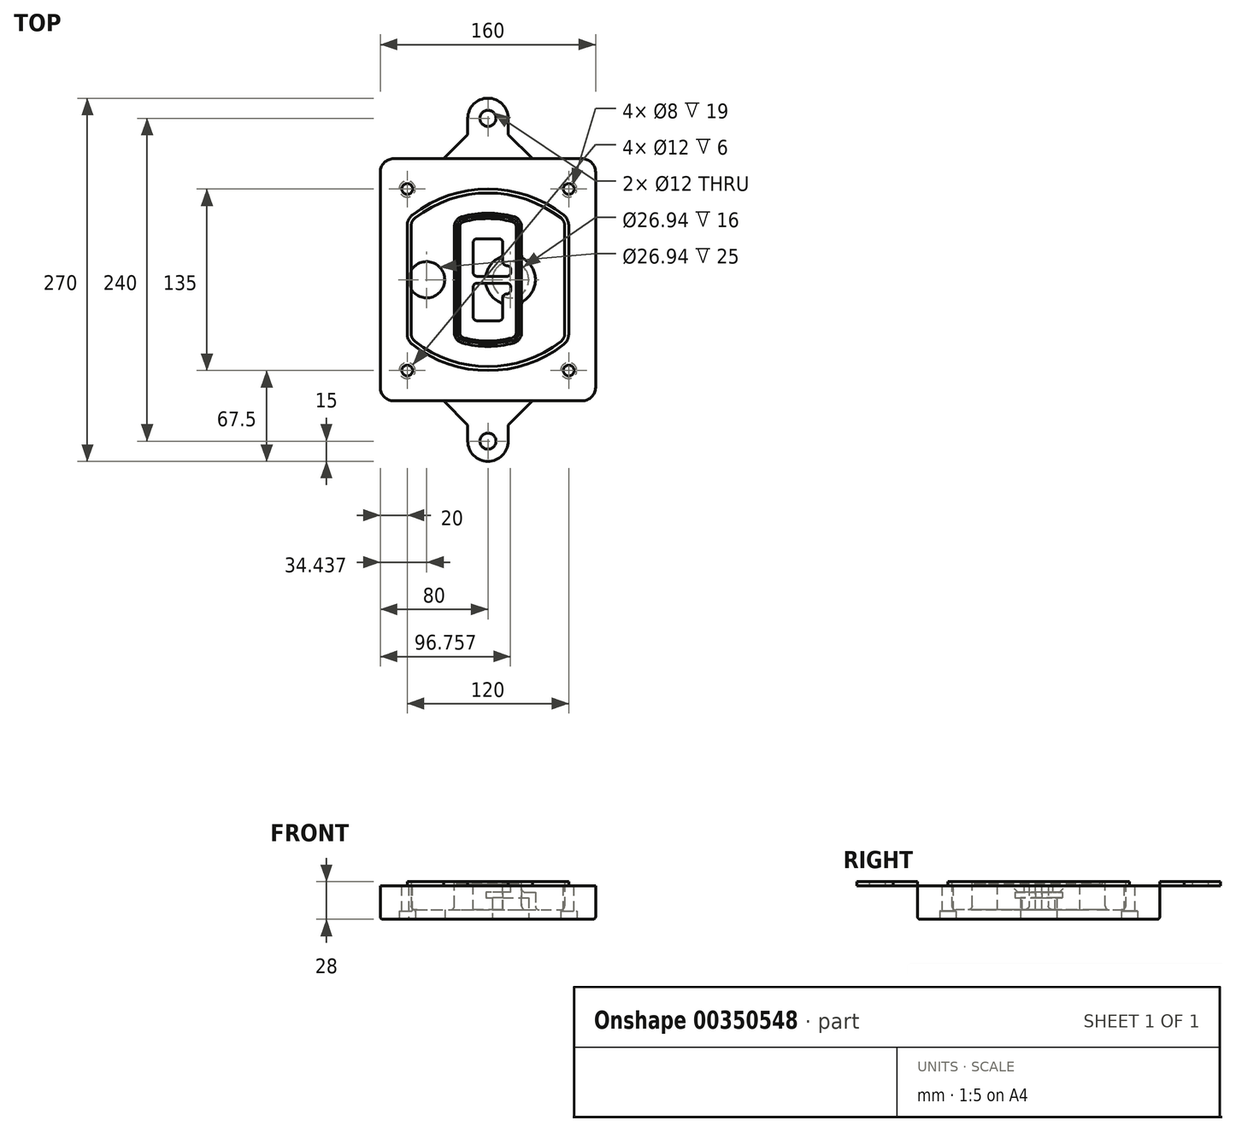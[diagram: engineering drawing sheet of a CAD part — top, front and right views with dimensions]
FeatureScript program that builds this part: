
annotation { "Feature Type Name" : "Feature", "Feature Type Description" : "" }
export const myFeature = defineFeature(function(context is Context, id is Id, definition is map)
    precondition{}
    {
        {
            var Q0;
            Q0=qCreatedBy(makeId("Top.planeOp"),FACE);
            var sketch = newSketch(context, id + "F0", { "sketchPlane" : qUnion([Q0])});
            skPoint(sketch, "E0.rect.middle", {"position": v(0, 0) * mm});
            skLineSegment(sketch, "E1.bottom", {"start": v(-70, -90) * mm, "end": v(70, -90) * mm});
            skLineSegment(sketch, "E1.top", {"start": v(-70, 90) * mm, "end": v(70, 90) * mm});
            skLineSegment(sketch, "E1.left", {"start": v(-80, -80) * mm, "end": v(-80, 80) * mm});
            skLineSegment(sketch, "E1.right", {"start": v(80, -80) * mm, "end": v(80, 80) * mm});
            skLineSegment(sketch, "E2", {"start": v(-80, 90) * mm, "end": v(80, -90) * mm, "construction": true});
            skLineSegment(sketch, "E3", {"start": v(80, 90) * mm, "end": v(-80, -90) * mm, "construction": true});
            skCircle(sketch, "E4", {"center": v(-60, 67.5) * mm, "radius": 4 * mm});
            skCircle(sketch, "E5", {"center": v(60, 67.5) * mm, "radius": 4 * mm});
            skCircle(sketch, "E6", {"center": v(60, -67.5) * mm, "radius": 4 * mm});
            skCircle(sketch, "E7", {"center": v(-60, -67.5) * mm, "radius": 4 * mm});
            skLineSegment(sketch, "E8", {"start": v(-60, 67.5) * mm, "end": v(60, 67.5) * mm, "construction": true});
            skLineSegment(sketch, "E9", {"start": v(60, 67.5) * mm, "end": v(60, -67.5) * mm, "construction": true});
            skLineSegment(sketch, "E10", {"start": v(60, -67.5) * mm, "end": v(-60, -67.5) * mm, "construction": true});
            skLineSegment(sketch, "E11", {"start": v(-60, -67.5) * mm, "end": v(-60, 67.5) * mm, "construction": true});
            skLineSegment(sketch, "E12", {"start": v(-60, 40.3) * mm, "end": v(-60, -40.3) * mm});
            skLineSegment(sketch, "E13", {"start": v(60, 40.3) * mm, "end": v(60, -40.3) * mm});
            skArc(sketch, "E14", {"start": v(56.15, 48.18) * mm, "mid": v(0, 67.5) * mm, "end": v(-56.15, 48.18) * mm});
            skArc(sketch, "E15", {"start": v(-56.15, -48.18) * mm, "mid": v(0, -67.5) * mm, "end": v(56.15, -48.18) * mm});
            skLineSegment(sketch, "E16", {"start": v(-60, 0) * mm, "end": v(60, 0) * mm, "construction": true});
            skPoint(sketch, "E17.visualSharp", {"position": v(-60, -45) * mm});
            skArc(sketch, "E17.filletArc", {"start": v(-60, -40.3) * mm, "mid": v(-58.99, -44.68) * mm, "end": v(-56.15, -48.18) * mm});
            skPoint(sketch, "E18.visualSharp", {"position": v(-60, 45) * mm});
            skArc(sketch, "E18.filletArc", {"start": v(-56.15, 48.18) * mm, "mid": v(-58.99, 44.68) * mm, "end": v(-60, 40.3) * mm});
            skPoint(sketch, "E19.visualSharp", {"position": v(60, 45) * mm});
            skArc(sketch, "E19.filletArc", {"start": v(60, 40.3) * mm, "mid": v(58.99, 44.68) * mm, "end": v(56.15, 48.18) * mm});
            skPoint(sketch, "E20.visualSharp", {"position": v(60, -45) * mm});
            skArc(sketch, "E20.filletArc", {"start": v(56.15, -48.18) * mm, "mid": v(58.99, -44.68) * mm, "end": v(60, -40.3) * mm});
            skPoint(sketch, "E21.visualSharp", {"position": v(-80, 90) * mm});
            skArc(sketch, "E21.filletArc", {"start": v(-70, 90) * mm, "mid": v(-77.07, 87.07) * mm, "end": v(-80, 80) * mm});
            skPoint(sketch, "E22.visualSharp", {"position": v(80, 90) * mm});
            skArc(sketch, "E22.filletArc", {"start": v(80, 80) * mm, "mid": v(77.07, 87.07) * mm, "end": v(70, 90) * mm});
            skPoint(sketch, "E23.visualSharp", {"position": v(80, -90) * mm});
            skArc(sketch, "E23.filletArc", {"start": v(70, -90) * mm, "mid": v(77.07, -87.07) * mm, "end": v(80, -80) * mm});
            skPoint(sketch, "E24.visualSharp", {"position": v(-80, -90) * mm});
            skArc(sketch, "E24.filletArc", {"start": v(-80, -80) * mm, "mid": v(-77.07, -87.07) * mm, "end": v(-70, -90) * mm});
            skArc(sketch, "E25.0", {"start": v(57, 40.3) * mm, "mid": v(56.3, 43.36) * mm, "end": v(54.3, 45.81) * mm});
            skLineSegment(sketch, "E25.1", {"start": v(57, 40.3) * mm, "end": v(57, -40.3) * mm});
            skArc(sketch, "E25.2", {"start": v(54.3, -45.81) * mm, "mid": v(56.3, -43.36) * mm, "end": v(57, -40.3) * mm});
            skArc(sketch, "E25.3", {"start": v(-54.3, -45.81) * mm, "mid": v(0, -64.5) * mm, "end": v(54.3, -45.81) * mm});
            skArc(sketch, "E25.4", {"start": v(-57, -40.3) * mm, "mid": v(-56.3, -43.36) * mm, "end": v(-54.3, -45.81) * mm});
            skArc(sketch, "E25.5", {"start": v(54.3, 45.81) * mm, "mid": v(0, 64.5) * mm, "end": v(-54.3, 45.81) * mm});
            skLineSegment(sketch, "E25.6", {"start": v(-57, 40.3) * mm, "end": v(-57, -40.3) * mm});
            skArc(sketch, "E25.7", {"start": v(-54.3, 45.81) * mm, "mid": v(-56.3, 43.36) * mm, "end": v(-57, 40.3) * mm});
            skArc(sketch, "E26.0", {"start": v(-58.62, 51.33) * mm, "mid": v(-62.58, 46.43) * mm, "end": v(-64, 40.3) * mm});
            skArc(sketch, "E26.1", {"start": v(58.62, 51.33) * mm, "mid": v(0, 71.5) * mm, "end": v(-58.62, 51.33) * mm});
            skArc(sketch, "E26.2", {"start": v(64, 40.3) * mm, "mid": v(62.58, 46.43) * mm, "end": v(58.62, 51.33) * mm});
            skLineSegment(sketch, "E26.3", {"start": v(64, 40.3) * mm, "end": v(64, -40.3) * mm});
            skArc(sketch, "E26.4", {"start": v(58.62, -51.33) * mm, "mid": v(62.58, -46.43) * mm, "end": v(64, -40.3) * mm});
            skLineSegment(sketch, "E26.5", {"start": v(-64, 40.3) * mm, "end": v(-64, -40.3) * mm});
            skArc(sketch, "E26.6", {"start": v(-58.62, -51.33) * mm, "mid": v(0, -71.5) * mm, "end": v(58.62, -51.33) * mm});
            skArc(sketch, "E26.7", {"start": v(-64, -40.3) * mm, "mid": v(-62.58, -46.43) * mm, "end": v(-58.62, -51.33) * mm});
            skSolve(sketch);
        }
        {
            var Q0;
            Q0=makeQuery(id+"F0.imprint","IMPRINT",FACE,{"disambiguationData":[TD([[makeQuery(id+"F0.imprint","IMPRINT",EDGE,{"derivedFrom":sQuery(id+"F0.wireOp",EDGE,"E1.bottom")}),1.0]])]});
            var Q1;
            Q1=makeQuery(id+"F0.imprint","IMPRINT",FACE,{"disambiguationData":[TD([[makeQuery(id+"F0.imprint","IMPRINT",EDGE,{"derivedFrom":sQuery(id+"F0.wireOp",EDGE,"E12")}),1.0]])]});
            var Q2;
            Q2=makeQuery(id+"F0.imprint","IMPRINT",FACE,{"disambiguationData":[TD([[makeQuery(id+"F0.imprint","IMPRINT",EDGE,{"derivedFrom":sQuery(id+"F0.wireOp",EDGE,"E25.0")}),1.0]])]});
            var Q3;
            Q3=makeQuery(id+"F0.imprint","IMPRINT",FACE,{"disambiguationData":[TD([[makeQuery(id+"F0.imprint","IMPRINT",EDGE,{"derivedFrom":sQuery(id+"F0.wireOp",EDGE,"E12")}),-1.0]])]});
            extrude(context, id + "F1", {"entities" : qUnion([Q0, Q1, Q2, Q3]), "oppositeDirection" : true, "depth" : 25 * mm});
        }
        {
            var Q0;
            Q0=makeQuery(id+"F0.imprint","IMPRINT",FACE,{"disambiguationData":[TD([[makeQuery(id+"F0.imprint","IMPRINT",EDGE,{"derivedFrom":sQuery(id+"F0.wireOp",EDGE,"E12")}),1.0]])]});
            extrude(context, id + "F2", {"entities" : qUnion([Q0]), "operationType" : NewBodyOperationType.ADD, "depth" : 3 * mm});
        }
        {
            var Q0;
            Q0=makeQuery(id+"F0.imprint","IMPRINT",FACE,{"disambiguationData":[TD([[makeQuery(id+"F0.imprint","IMPRINT",EDGE,{"derivedFrom":sQuery(id+"F0.wireOp",EDGE,"E25.0")}),1.0]])]});
            extrude(context, id + "F3", {"entities" : qUnion([Q0]), "operationType" : NewBodyOperationType.REMOVE, "oppositeDirection" : true, "depth" : 18 * mm});
        }
        {
            var Q0;
            Q0=makeQuery(id+"F2.opExtrude","CAP_FACE",FACE,{"disambiguationData":[OSD([sQuery(id+"F0.wireOp",EDGE,"E12"),sQuery(id+"F0.wireOp",EDGE,"E13"),sQuery(id+"F0.wireOp",EDGE,"E14"),sQuery(id+"F0.wireOp",EDGE,"E15"),sQuery(id+"F0.wireOp",EDGE,"E17.filletArc"),sQuery(id+"F0.wireOp",EDGE,"E18.filletArc"),sQuery(id+"F0.wireOp",EDGE,"E19.filletArc"),sQuery(id+"F0.wireOp",EDGE,"E20.filletArc"),sQuery(id+"F0.wireOp",EDGE,"E25.0"),sQuery(id+"F0.wireOp",EDGE,"E25.1"),sQuery(id+"F0.wireOp",EDGE,"E25.2"),sQuery(id+"F0.wireOp",EDGE,"E25.3"),sQuery(id+"F0.wireOp",EDGE,"E25.4"),sQuery(id+"F0.wireOp",EDGE,"E25.5"),sQuery(id+"F0.wireOp",EDGE,"E25.6"),sQuery(id+"F0.wireOp",EDGE,"E25.7")])],"isStart":false});
            var sketch = newSketch(context, id + "F4", { "sketchPlane" : qUnion([Q0])});
            skArc(sketch, "E27.0", {"start": v(-19.08, -46.97) * mm, "mid": v(0, -49.5) * mm, "end": v(19.08, -46.97) * mm});
            skArc(sketch, "E28.0", {"start": v(19.08, 46.97) * mm, "mid": v(0, 49.5) * mm, "end": v(-19.08, 46.97) * mm});
            skLineSegment(sketch, "E29", {"start": v(-25, 39.25) * mm, "end": v(-25, -39.25) * mm});
            skLineSegment(sketch, "E30", {"start": v(25, 39.25) * mm, "end": v(25, -39.25) * mm});
            skLineSegment(sketch, "E31", {"start": v(-25, 45.1) * mm, "end": v(25, 45.1) * mm, "construction": true});
            skLineSegment(sketch, "E32", {"start": v(-25, -45.1) * mm, "end": v(25, -45.1) * mm, "construction": true});
            skPoint(sketch, "E33.visualSharp", {"position": v(-25, 45.1) * mm});
            skArc(sketch, "E33.filletArc", {"start": v(-19.08, 46.97) * mm, "mid": v(-23.35, 44.11) * mm, "end": v(-25, 39.25) * mm});
            skPoint(sketch, "E34.visualSharp", {"position": v(25, 45.1) * mm});
            skArc(sketch, "E34.filletArc", {"start": v(25, 39.25) * mm, "mid": v(23.35, 44.11) * mm, "end": v(19.08, 46.97) * mm});
            skPoint(sketch, "E35.visualSharp", {"position": v(25, -45.1) * mm});
            skArc(sketch, "E35.filletArc", {"start": v(19.08, -46.97) * mm, "mid": v(23.35, -44.11) * mm, "end": v(25, -39.25) * mm});
            skPoint(sketch, "E36.visualSharp", {"position": v(-25, -45.1) * mm});
            skArc(sketch, "E36.filletArc", {"start": v(-25, -39.25) * mm, "mid": v(-23.35, -44.11) * mm, "end": v(-19.08, -46.97) * mm});
            skArc(sketch, "E37.0", {"start": v(54.3, 45.81) * mm, "mid": v(0, 64.5) * mm, "end": v(-54.3, 45.81) * mm});
            skArc(sketch, "E37.1", {"start": v(-54.3, 45.81) * mm, "mid": v(-56.3, 43.36) * mm, "end": v(-57, 40.3) * mm});
            skLineSegment(sketch, "E37.2", {"start": v(-57, 40.3) * mm, "end": v(-57, -40.3) * mm});
            skArc(sketch, "E37.3", {"start": v(-57, -40.3) * mm, "mid": v(-56.3, -43.36) * mm, "end": v(-54.3, -45.81) * mm});
            skArc(sketch, "E37.4", {"start": v(-54.3, -45.81) * mm, "mid": v(0, -64.5) * mm, "end": v(54.3, -45.81) * mm});
            skArc(sketch, "E37.5", {"start": v(54.3, -45.81) * mm, "mid": v(56.3, -43.36) * mm, "end": v(57, -40.3) * mm});
            skLineSegment(sketch, "E37.6", {"start": v(57, 40.3) * mm, "end": v(57, -40.3) * mm});
            skArc(sketch, "E37.7", {"start": v(57, 40.3) * mm, "mid": v(56.3, 43.36) * mm, "end": v(54.3, 45.81) * mm});
            skLineSegment(sketch, "E38.0", {"start": v(23, 39.25) * mm, "end": v(23, -39.25) * mm});
            skArc(sketch, "E38.1", {"start": v(18.56, -45.04) * mm, "mid": v(21.76, -42.9) * mm, "end": v(23, -39.25) * mm});
            skArc(sketch, "E38.2", {"start": v(-18.56, -45.04) * mm, "mid": v(0, -47.5) * mm, "end": v(18.56, -45.04) * mm});
            skArc(sketch, "E38.3", {"start": v(-23, -39.25) * mm, "mid": v(-21.76, -42.9) * mm, "end": v(-18.56, -45.04) * mm});
            skLineSegment(sketch, "E38.4", {"start": v(-23, 39.25) * mm, "end": v(-23, -39.25) * mm});
            skArc(sketch, "E38.5", {"start": v(23, 39.25) * mm, "mid": v(21.76, 42.9) * mm, "end": v(18.56, 45.04) * mm});
            skArc(sketch, "E38.6", {"start": v(-18.56, 45.04) * mm, "mid": v(-21.76, 42.9) * mm, "end": v(-23, 39.25) * mm});
            skArc(sketch, "E38.7", {"start": v(18.56, 45.04) * mm, "mid": v(0, 47.5) * mm, "end": v(-18.56, 45.04) * mm});
            skArc(sketch, "E39.0", {"start": v(21, 39.25) * mm, "mid": v(20.18, 41.68) * mm, "end": v(18.04, 43.1) * mm});
            skLineSegment(sketch, "E39.1", {"start": v(21, 39.25) * mm, "end": v(21, -39.25) * mm});
            skArc(sketch, "E39.2", {"start": v(18.04, -43.1) * mm, "mid": v(20.18, -41.68) * mm, "end": v(21, -39.25) * mm});
            skArc(sketch, "E39.3", {"start": v(-18.04, -43.1) * mm, "mid": v(0, -45.5) * mm, "end": v(18.04, -43.1) * mm});
            skArc(sketch, "E39.4", {"start": v(-21, -39.25) * mm, "mid": v(-20.18, -41.68) * mm, "end": v(-18.04, -43.1) * mm});
            skArc(sketch, "E39.5", {"start": v(18.04, 43.1) * mm, "mid": v(0, 45.5) * mm, "end": v(-18.04, 43.1) * mm});
            skLineSegment(sketch, "E39.6", {"start": v(-21, 39.25) * mm, "end": v(-21, -39.25) * mm});
            skArc(sketch, "E39.7", {"start": v(-18.04, 43.1) * mm, "mid": v(-20.18, 41.68) * mm, "end": v(-21, 39.25) * mm});
            skLineSegment(sketch, "E40", {"start": v(-25, 0) * mm, "end": v(25, 0) * mm, "construction": true});
            skLineSegment(sketch, "E41", {"start": v(-11, 5.5) * mm, "end": v(-11, 27.5) * mm});
            skLineSegment(sketch, "E42", {"start": v(-8, 30.5) * mm, "end": v(8, 30.5) * mm});
            skLineSegment(sketch, "E43", {"start": v(11, 27.5) * mm, "end": v(11, 13.5) * mm});
            skLineSegment(sketch, "E44", {"start": v(14, 10.5) * mm, "end": v(14, 10.5) * mm});
            skLineSegment(sketch, "E45", {"start": v(17, 7.5) * mm, "end": v(17, 5.5) * mm});
            skLineSegment(sketch, "E46", {"start": v(14, 2.5) * mm, "end": v(-8, 2.5) * mm});
            skPoint(sketch, "E47.visualSharp", {"position": v(-11, 30.5) * mm});
            skArc(sketch, "E47.filletArc", {"start": v(-8, 30.5) * mm, "mid": v(-10.12, 29.62) * mm, "end": v(-11, 27.5) * mm});
            skPoint(sketch, "E48.visualSharp", {"position": v(11, 30.5) * mm});
            skArc(sketch, "E48.filletArc", {"start": v(11, 27.5) * mm, "mid": v(10.12, 29.62) * mm, "end": v(8, 30.5) * mm});
            skPoint(sketch, "E49.visualSharp", {"position": v(11, 10.5) * mm});
            skArc(sketch, "E49.filletArc", {"start": v(11, 13.5) * mm, "mid": v(11.88, 11.38) * mm, "end": v(14, 10.5) * mm});
            skPoint(sketch, "E50.visualSharp", {"position": v(17, 10.5) * mm});
            skArc(sketch, "E50.filletArc", {"start": v(17, 7.5) * mm, "mid": v(16.12, 9.62) * mm, "end": v(14, 10.5) * mm});
            skPoint(sketch, "E51.visualSharp", {"position": v(17, 2.5) * mm});
            skArc(sketch, "E51.filletArc", {"start": v(14, 2.5) * mm, "mid": v(16.12, 3.38) * mm, "end": v(17, 5.5) * mm});
            skPoint(sketch, "E52.visualSharp", {"position": v(-11, 2.5) * mm});
            skArc(sketch, "E52.filletArc", {"start": v(-11, 5.5) * mm, "mid": v(-10.12, 3.38) * mm, "end": v(-8, 2.5) * mm});
            skLineSegment(sketch, "E53.0.MirrorCS", {"start": v(14, -2.5) * mm, "end": v(-8, -2.5) * mm});
            skArc(sketch, "E54.0.MirrorCS", {"start": v(-11, -5.5) * mm, "mid": v(-10.12, -3.38) * mm, "end": v(-8, -2.5) * mm});
            skLineSegment(sketch, "E55.0.MirrorCS", {"start": v(-11, -5.5) * mm, "end": v(-11, -27.5) * mm});
            skArc(sketch, "E56.0.MirrorCS", {"start": v(-8, -30.5) * mm, "mid": v(-10.12, -29.62) * mm, "end": v(-11, -27.5) * mm});
            skLineSegment(sketch, "E57.0.MirrorCS", {"start": v(-8, -30.5) * mm, "end": v(8, -30.5) * mm});
            skArc(sketch, "E58.0.MirrorCS", {"start": v(11, -27.5) * mm, "mid": v(10.12, -29.62) * mm, "end": v(8, -30.5) * mm});
            skLineSegment(sketch, "E59.0.MirrorCS", {"start": v(11, -27.5) * mm, "end": v(11, -13.5) * mm});
            skArc(sketch, "E60.0.MirrorCS", {"start": v(11, -13.5) * mm, "mid": v(11.88, -11.38) * mm, "end": v(14, -10.5) * mm});
            skArc(sketch, "E61.0.MirrorCS", {"start": v(17, -7.5) * mm, "mid": v(16.12, -9.62) * mm, "end": v(14, -10.5) * mm});
            skLineSegment(sketch, "E62.0.MirrorCS", {"start": v(17, -7.5) * mm, "end": v(17, -5.5) * mm});
            skArc(sketch, "E63.0.MirrorCS", {"start": v(14, -2.5) * mm, "mid": v(16.12, -3.38) * mm, "end": v(17, -5.5) * mm});
            skSolve(sketch);
        }
        {
            var Q0;
            Q0=makeQuery(id+"F4.imprint","IMPRINT",FACE,{"disambiguationData":[TD([[makeQuery(id+"F4.imprint","IMPRINT",EDGE,{"derivedFrom":sQuery(id+"F4.wireOp",EDGE,"E27.0")}),1.0]])]});
            var Q1;
            Q1=makeQuery(id+"F4.imprint","IMPRINT",FACE,{"disambiguationData":[TD([[makeQuery(id+"F4.imprint","IMPRINT",EDGE,{"derivedFrom":sQuery(id+"F4.wireOp",EDGE,"E38.0")}),-1.0]])]});
            var Q2;
            Q2=makeQuery(id+"F4.imprint","IMPRINT",FACE,{"disambiguationData":[TD([[makeQuery(id+"F4.imprint","IMPRINT",EDGE,{"derivedFrom":sQuery(id+"F4.wireOp",EDGE,"E39.0")}),1.0]])]});
            extrude(context, id + "F5", {"entities" : qUnion([Q0, Q1, Q2]), "operationType" : NewBodyOperationType.ADD, "endBound" : BoundingType.UP_TO_NEXT, "oppositeDirection" : true, "depth" : 25 * mm});
        }
        {
            var Q0;
            Q0=makeQuery(id+"F4.imprint","IMPRINT",FACE,{"disambiguationData":[TD([[makeQuery(id+"F4.imprint","IMPRINT",EDGE,{"derivedFrom":sQuery(id+"F4.wireOp",EDGE,"E38.0")}),-1.0]])]});
            extrude(context, id + "F6", {"entities" : qUnion([Q0]), "operationType" : NewBodyOperationType.REMOVE, "oppositeDirection" : true, "depth" : 2 * mm});
        }
        {
            var Q0;
            Q0=makeQuery(id+"F1.opExtrude","CAP_FACE",FACE,{"disambiguationData":[OSD([sQuery(id+"F0.wireOp",EDGE,"E1.bottom"),sQuery(id+"F0.wireOp",EDGE,"E1.top"),sQuery(id+"F0.wireOp",EDGE,"E1.left"),sQuery(id+"F0.wireOp",EDGE,"E1.right"),sQuery(id+"F0.wireOp",EDGE,"E4"),sQuery(id+"F0.wireOp",EDGE,"E5"),sQuery(id+"F0.wireOp",EDGE,"E6"),sQuery(id+"F0.wireOp",EDGE,"E7"),sQuery(id+"F0.wireOp",EDGE,"E21.filletArc"),sQuery(id+"F0.wireOp",EDGE,"E22.filletArc"),sQuery(id+"F0.wireOp",EDGE,"E23.filletArc"),sQuery(id+"F0.wireOp",EDGE,"E24.filletArc")])],"isStart":false});
            var sketch = newSketch(context, id + "F7", { "sketchPlane" : qUnion([Q0])});
            skCircle(sketch, "E64", {"center": v(16.76, 0) * mm, "radius": 13.47 * mm});
            skCircle(sketch, "E65", {"center": v(-45.56, 0) * mm, "radius": 13.47 * mm});
            skLineSegment(sketch, "E66", {"start": v(80, 0) * mm, "end": v(-80, 0) * mm});
            skCircle(sketch, "E67", {"center": v(16.76, 0) * mm, "radius": 18.47 * mm});
            skCircle(sketch, "E68", {"center": v(60, -67.5) * mm, "radius": 6 * mm});
            skCircle(sketch, "E69", {"center": v(-60, -67.5) * mm, "radius": 6 * mm});
            skCircle(sketch, "E70", {"center": v(-60, 67.5) * mm, "radius": 6 * mm});
            skCircle(sketch, "E71", {"center": v(60, 67.5) * mm, "radius": 6 * mm});
            skSolve(sketch);
        }
        {
            var Q0;
            {var subQ1=sQuery(id+"F7.wireOp",EDGE,"E66");var subQ4=sQuery(id+"F7.wireOp",EDGE,"E64");var subQ6=makeQuery(id+"F7.imprint","INTERSECT",VERTEX,{"disambiguationData":[OD(0.0)],"derivedFrom":[subQ4,subQ1]});Q0=makeQuery(id+"F7.imprint","IMPRINT",FACE,{"disambiguationData":[TD([[makeQuery(id+"F7.imprint","IMPRINT",EDGE,{"disambiguationData":[TD([[subQ6,-1.0]])],"derivedFrom":subQ4}),-1.0]])]});}
            var Q1;
            {var subQ0=sQuery(id+"F7.wireOp",EDGE,"E66");var subQ1=sQuery(id+"F7.wireOp",EDGE,"E64");var subQ3=makeQuery(id+"F7.imprint","INTERSECT",VERTEX,{"disambiguationData":[OD(0.0)],"derivedFrom":[subQ1,subQ0]});Q1=makeQuery(id+"F7.imprint","IMPRINT",FACE,{"disambiguationData":[TD([[makeQuery(id+"F7.imprint","IMPRINT",EDGE,{"disambiguationData":[TD([[subQ3,-1.0]])],"derivedFrom":subQ1}),1.0]])]});}
            var Q2;
            {var subQ0=sQuery(id+"F7.wireOp",EDGE,"E66");var subQ1=sQuery(id+"F7.wireOp",EDGE,"E64");var subQ3=makeQuery(id+"F7.imprint","INTERSECT",VERTEX,{"disambiguationData":[OD(0.0)],"derivedFrom":[subQ1,subQ0]});Q2=makeQuery(id+"F7.imprint","IMPRINT",FACE,{"disambiguationData":[TD([[makeQuery(id+"F7.imprint","IMPRINT",EDGE,{"disambiguationData":[TD([[subQ3,1.0]])],"derivedFrom":subQ1}),1.0]])]});}
            var Q3;
            {var subQ1=sQuery(id+"F7.wireOp",EDGE,"E66");var subQ4=sQuery(id+"F7.wireOp",EDGE,"E64");var subQ6=makeQuery(id+"F7.imprint","INTERSECT",VERTEX,{"disambiguationData":[OD(0.0)],"derivedFrom":[subQ4,subQ1]});Q3=makeQuery(id+"F7.imprint","IMPRINT",FACE,{"disambiguationData":[TD([[makeQuery(id+"F7.imprint","IMPRINT",EDGE,{"disambiguationData":[TD([[subQ6,1.0]])],"derivedFrom":subQ4}),-1.0]])]});}
            extrude(context, id + "F8", {"entities" : qUnion([Q0, Q1, Q2, Q3]), "operationType" : NewBodyOperationType.ADD, "oppositeDirection" : true, "depth" : 20 * mm});
        }
        {
            var Q0;
            {var subQ0=sQuery(id+"F7.wireOp",EDGE,"E66");var subQ1=sQuery(id+"F7.wireOp",EDGE,"E64");var subQ3=makeQuery(id+"F7.imprint","INTERSECT",VERTEX,{"disambiguationData":[OD(0.0)],"derivedFrom":[subQ1,subQ0]});Q0=makeQuery(id+"F7.imprint","IMPRINT",FACE,{"disambiguationData":[TD([[makeQuery(id+"F7.imprint","IMPRINT",EDGE,{"disambiguationData":[TD([[subQ3,-1.0]])],"derivedFrom":subQ1}),1.0]])]});}
            var Q1;
            {var subQ0=sQuery(id+"F7.wireOp",EDGE,"E66");var subQ1=sQuery(id+"F7.wireOp",EDGE,"E64");var subQ3=makeQuery(id+"F7.imprint","INTERSECT",VERTEX,{"disambiguationData":[OD(0.0)],"derivedFrom":[subQ1,subQ0]});Q1=makeQuery(id+"F7.imprint","IMPRINT",FACE,{"disambiguationData":[TD([[makeQuery(id+"F7.imprint","IMPRINT",EDGE,{"disambiguationData":[TD([[subQ3,1.0]])],"derivedFrom":subQ1}),1.0]])]});}
            extrude(context, id + "F9", {"entities" : qUnion([Q0, Q1]), "operationType" : NewBodyOperationType.REMOVE, "oppositeDirection" : true, "depth" : 16 * mm});
        }
        {
            var Q0;
            {var subQ0=sQuery(id+"F7.wireOp",EDGE,"E66");var subQ1=sQuery(id+"F7.wireOp",EDGE,"E65");var subQ3=makeQuery(id+"F7.imprint","INTERSECT",VERTEX,{"disambiguationData":[OD(0.0)],"derivedFrom":[subQ1,subQ0]});Q0=makeQuery(id+"F7.imprint","IMPRINT",FACE,{"disambiguationData":[TD([[makeQuery(id+"F7.imprint","IMPRINT",EDGE,{"disambiguationData":[TD([[subQ3,-1.0]])],"derivedFrom":subQ1}),1.0]])]});}
            var Q1;
            {var subQ0=sQuery(id+"F7.wireOp",EDGE,"E66");var subQ1=sQuery(id+"F7.wireOp",EDGE,"E65");var subQ3=makeQuery(id+"F7.imprint","INTERSECT",VERTEX,{"disambiguationData":[OD(0.0)],"derivedFrom":[subQ1,subQ0]});Q1=makeQuery(id+"F7.imprint","IMPRINT",FACE,{"disambiguationData":[TD([[makeQuery(id+"F7.imprint","IMPRINT",EDGE,{"disambiguationData":[TD([[subQ3,1.0]])],"derivedFrom":subQ1}),1.0]])]});}
            extrude(context, id + "F10", {"entities" : qUnion([Q0, Q1]), "operationType" : NewBodyOperationType.REMOVE, "oppositeDirection" : true, "depth" : 25 * mm});
        }
        {
            var Q0;
            Q0=makeQuery(id+"F7.imprint","IMPRINT",FACE,{"disambiguationData":[TD([[makeQuery(id+"F7.imprint","IMPRINT",EDGE,{"derivedFrom":sQuery(id+"F7.wireOp",EDGE,"E68")}),1.0]])]});
            var Q1;
            Q1=makeQuery(id+"F7.imprint","IMPRINT",FACE,{"disambiguationData":[TD([[makeQuery(id+"F7.imprint","IMPRINT",EDGE,{"derivedFrom":makeQuery(id+"F1.opExtrude","CAP_EDGE",EDGE,{"disambiguationData":[OSD([sQuery(id+"F0.wireOp",EDGE,"E5")])],"isStart":false})}),-1.0]])]});
            var Q2;
            Q2=makeQuery(id+"F7.imprint","IMPRINT",FACE,{"disambiguationData":[TD([[makeQuery(id+"F7.imprint","IMPRINT",EDGE,{"derivedFrom":sQuery(id+"F7.wireOp",EDGE,"E69")}),1.0]])]});
            var Q3;
            Q3=makeQuery(id+"F7.imprint","IMPRINT",FACE,{"disambiguationData":[TD([[makeQuery(id+"F7.imprint","IMPRINT",EDGE,{"derivedFrom":makeQuery(id+"F1.opExtrude","CAP_EDGE",EDGE,{"disambiguationData":[OSD([sQuery(id+"F0.wireOp",EDGE,"E4")])],"isStart":false})}),-1.0]])]});
            var Q4;
            Q4=makeQuery(id+"F7.imprint","IMPRINT",FACE,{"disambiguationData":[TD([[makeQuery(id+"F7.imprint","IMPRINT",EDGE,{"derivedFrom":sQuery(id+"F7.wireOp",EDGE,"E70")}),1.0]])]});
            var Q5;
            Q5=makeQuery(id+"F7.imprint","IMPRINT",FACE,{"disambiguationData":[TD([[makeQuery(id+"F7.imprint","IMPRINT",EDGE,{"derivedFrom":makeQuery(id+"F1.opExtrude","CAP_EDGE",EDGE,{"disambiguationData":[OSD([sQuery(id+"F0.wireOp",EDGE,"E7")])],"isStart":false})}),-1.0]])]});
            var Q6;
            Q6=makeQuery(id+"F7.imprint","IMPRINT",FACE,{"disambiguationData":[TD([[makeQuery(id+"F7.imprint","IMPRINT",EDGE,{"derivedFrom":sQuery(id+"F7.wireOp",EDGE,"E71")}),1.0]])]});
            var Q7;
            Q7=makeQuery(id+"F7.imprint","IMPRINT",FACE,{"disambiguationData":[TD([[makeQuery(id+"F7.imprint","IMPRINT",EDGE,{"derivedFrom":makeQuery(id+"F1.opExtrude","CAP_EDGE",EDGE,{"disambiguationData":[OSD([sQuery(id+"F0.wireOp",EDGE,"E6")])],"isStart":false})}),-1.0]])]});
            extrude(context, id + "F11", {"entities" : qUnion([Q0, Q1, Q2, Q3, Q4, Q5, Q6, Q7]), "operationType" : NewBodyOperationType.REMOVE, "oppositeDirection" : true, "depth" : 6 * mm});
        }
        {
            var Q0;
            Q0=makeQuery(id+"F9.boolean.opBoolean","COPY",FACE,{"derivedFrom":makeQuery(id+"F9.opExtrude","CAP_FACE",FACE,{"disambiguationData":[OSD([sQuery(id+"F7.wireOp",EDGE,"E64")])],"isStart":false})});
            var sketch = newSketch(context, id + "F12", { "sketchPlane" : qUnion([Q0])});
            skArc(sketch, "E72.0", {"start": v(11, 17.55) * mm, "mid": v(2.57, 11.82) * mm, "end": v(-1.54, 2.5) * mm});
            skArc(sketch, "E72.1", {"start": v(-1.54, -2.5) * mm, "mid": v(2.57, -11.82) * mm, "end": v(11, -17.55) * mm});
            skLineSegment(sketch, "E73", {"start": v(-1.54, -2.5) * mm, "end": v(14, -2.5) * mm});
            skLineSegment(sketch, "E74.0", {"start": v(14, 2.5) * mm, "end": v(-1.54, 2.5) * mm});
            skArc(sketch, "E74.1", {"start": v(14, 2.5) * mm, "mid": v(16.12, 3.38) * mm, "end": v(17, 5.5) * mm});
            skLineSegment(sketch, "E74.2", {"start": v(17, 7.5) * mm, "end": v(17, 5.5) * mm});
            skArc(sketch, "E74.3", {"start": v(17, 7.5) * mm, "mid": v(16.12, 9.62) * mm, "end": v(14, 10.5) * mm});
            skArc(sketch, "E74.4", {"start": v(11, 13.5) * mm, "mid": v(11.88, 11.38) * mm, "end": v(14, 10.5) * mm});
            skLineSegment(sketch, "E74.5", {"start": v(11, 17.55) * mm, "end": v(11, 13.5) * mm});
            skLineSegment(sketch, "E74.7", {"start": v(14, -2.5) * mm, "end": v(-1.54, -2.5) * mm});
            skArc(sketch, "E74.8", {"start": v(14, -2.5) * mm, "mid": v(16.12, -3.38) * mm, "end": v(17, -5.5) * mm});
            skLineSegment(sketch, "E74.9", {"start": v(17, -7.5) * mm, "end": v(17, -5.5) * mm});
            skArc(sketch, "E74.10", {"start": v(17, -7.5) * mm, "mid": v(16.12, -9.62) * mm, "end": v(14, -10.5) * mm});
            skArc(sketch, "E74.11", {"start": v(11, -13.5) * mm, "mid": v(11.88, -11.38) * mm, "end": v(14, -10.5) * mm});
            skLineSegment(sketch, "E74.12", {"start": v(11, -17.55) * mm, "end": v(11, -13.5) * mm});
            skPoint(sketch, "E75.orphan", {"position": v(11, -27.5) * mm});
            skPoint(sketch, "E76.orphan", {"position": v(-8, -2.5) * mm});
            skPoint(sketch, "E77.orphan", {"position": v(-8, 2.5) * mm});
            skPoint(sketch, "E78.orphan", {"position": v(11, 27.5) * mm});
            skSolve(sketch);
        }
        {
            var Q0;
            {var subQ7=sQuery(id+"F12.wireOp",EDGE,"E72.0");var subQ14=sQuery(id+"F12.wireOp",EDGE,"E72.1");var subQ16=sQuery(id+"F12.wireOp",EDGE,"E74.1");var subQ18=sQuery(id+"F12.wireOp",EDGE,"E74.8");Q0=qUnion([makeQuery(id+"F12.imprint","IMPRINT",FACE,{"disambiguationData":[TD([[makeQuery(id+"F12.imprint","IMPRINT",EDGE,{"derivedFrom":subQ7}),1.0]])]}),makeQuery(id+"F12.imprint","IMPRINT",FACE,{"disambiguationData":[TD([[makeQuery(id+"F12.imprint","IMPRINT",EDGE,{"derivedFrom":subQ14}),1.0]])]}),makeQuery(id+"F12.imprint","IMPRINT",FACE,{"disambiguationData":[TD([[makeQuery(id+"F12.imprint","IMPRINT",EDGE,{"derivedFrom":subQ16}),1.0]])]}),makeQuery(id+"F12.imprint","IMPRINT",FACE,{"disambiguationData":[TD([[makeQuery(id+"F12.imprint","IMPRINT",EDGE,{"derivedFrom":subQ18}),-1.0]])]})]);}
            var Q1;
            Q1=makeQuery(id+"F5.boolean.opBoolean","SPLIT",FACE,{"disambiguationData":[TD([makeQuery(id+"F5.opExtrude","SWEPT_FACE",FACE,{"disambiguationData":[OSD([sQuery(id+"F4.wireOp",EDGE,"E41")])]})])],"derivedFrom":makeQuery(id+"F3.boolean.opBoolean","COPY",FACE,{"derivedFrom":makeQuery(id+"F3.opExtrude","CAP_FACE",FACE,{"disambiguationData":[OSD([sQuery(id+"F0.wireOp",EDGE,"E25.0"),sQuery(id+"F0.wireOp",EDGE,"E25.1"),sQuery(id+"F0.wireOp",EDGE,"E25.2"),sQuery(id+"F0.wireOp",EDGE,"E25.3"),sQuery(id+"F0.wireOp",EDGE,"E25.4"),sQuery(id+"F0.wireOp",EDGE,"E25.5"),sQuery(id+"F0.wireOp",EDGE,"E25.6"),sQuery(id+"F0.wireOp",EDGE,"E25.7")])],"isStart":false})})});
            extrude(context, id + "F13", {"entities" : qUnion([Q0]), "operationType" : NewBodyOperationType.REMOVE, "endBound" : BoundingType.UP_TO_SURFACE, "endBoundEntityFace" : qUnion([Q1]), "depth" : 25 * mm});
        }
        {
            var Q0;
            Q0=makeQuery(id+"F3.boolean.opBoolean","COPY",EDGE,{"derivedFrom":makeQuery(id+"F3.opExtrude","CAP_EDGE",EDGE,{"disambiguationData":[OSD([sQuery(id+"F0.wireOp",EDGE,"E25.6")])],"isStart":false})});
            var Q1;
            Q1=makeQuery(id+"F8.boolean.opBoolean","INTERSECT",EDGE,{"derivedFrom":[makeQuery(id+"F5.opExtrude","SWEPT_FACE",FACE,{"disambiguationData":[OSD([sQuery(id+"F4.wireOp",EDGE,"E30")])]}),makeQuery(id+"F8.opExtrude","CAP_FACE",FACE,{"disambiguationData":[OSD([sQuery(id+"F7.wireOp",EDGE,"E67")])],"isStart":false})]});
            var Q2;
            Q2=makeQuery(id+"F8.boolean.opBoolean","INTERSECT",EDGE,{"disambiguationData":[OD(1.0)],"derivedFrom":[makeQuery(id+"F5.opExtrude","SWEPT_FACE",FACE,{"disambiguationData":[OSD([sQuery(id+"F4.wireOp",EDGE,"E30")])]}),makeQuery(id+"F8.opExtrude","SWEPT_FACE",FACE,{"disambiguationData":[OSD([sQuery(id+"F7.wireOp",EDGE,"E67")])]})]});
            var Q3;
            {var subQ0=sQuery(id+"F4.wireOp",EDGE,"E30");Q3=makeQuery(id+"F8.boolean.opBoolean","SPLIT",EDGE,{"disambiguationData":[TD([makeQuery(id+"F5.opExtrude","SWEPT_FACE",FACE,{"disambiguationData":[OSD([sQuery(id+"F4.wireOp",EDGE,"E35.filletArc")])]})])],"derivedFrom":makeQuery(id+"F5.opExtrude","CAP_EDGE",EDGE,{"disambiguationData":[OSD([subQ0])],"isStart":false})});}
            var Q4;
            {var subQ0=sQuery(id+"F0.wireOp",EDGE,"E25.7");var subQ1=sQuery(id+"F0.wireOp",EDGE,"E25.1");var subQ2=sQuery(id+"F0.wireOp",EDGE,"E25.6");var subQ3=sQuery(id+"F0.wireOp",EDGE,"E25.5");var subQ4=sQuery(id+"F0.wireOp",EDGE,"E25.4");var subQ5=sQuery(id+"F0.wireOp",EDGE,"E25.0");var subQ6=sQuery(id+"F0.wireOp",EDGE,"E25.2");var subQ7=sQuery(id+"F0.wireOp",EDGE,"E25.3");Q4=makeQuery(id+"F8.boolean.opBoolean","INTERSECT",EDGE,{"derivedFrom":[makeQuery(id+"F5.boolean.opBoolean","SPLIT",FACE,{"disambiguationData":[TD([makeQuery(id+"F2.opExtrude","SWEPT_FACE",FACE,{"disambiguationData":[OSD([subQ5])]})])],"derivedFrom":makeQuery(id+"F3.boolean.opBoolean","COPY",FACE,{"derivedFrom":makeQuery(id+"F3.opExtrude","CAP_FACE",FACE,{"disambiguationData":[OSD([subQ5,subQ1,subQ6,subQ7,subQ4,subQ3,subQ2,subQ0])],"isStart":false})})}),makeQuery(id+"F8.opExtrude","SWEPT_FACE",FACE,{"disambiguationData":[OSD([sQuery(id+"F7.wireOp",EDGE,"E67")])]})]});}
            var Q5;
            Q5=makeQuery(id+"F8.boolean.opBoolean","INTERSECT",EDGE,{"disambiguationData":[OD(0.0)],"derivedFrom":[makeQuery(id+"F5.opExtrude","SWEPT_FACE",FACE,{"disambiguationData":[OSD([sQuery(id+"F4.wireOp",EDGE,"E30")])]}),makeQuery(id+"F8.opExtrude","SWEPT_FACE",FACE,{"disambiguationData":[OSD([sQuery(id+"F7.wireOp",EDGE,"E67")])]})]});
            fillet(context, id + "F14", {"entities" : qUnion([Q0, Q1, Q2, Q3, Q4, Q5]), "radius" : 3 * mm, "tangentPropagation" : true, "allowEdgeOverflow" : false});
        }
        {
            var Q0;
            Q0=makeQuery(id+"F1.opExtrude","CAP_EDGE",EDGE,{"disambiguationData":[OSD([sQuery(id+"F0.wireOp",EDGE,"E1.bottom")])],"isStart":false});
            fillet(context, id + "F15", {"entities" : qUnion([Q0]), "radius" : 2 * mm, "tangentPropagation" : true, "allowEdgeOverflow" : false});
        }
        {
            var Q0;
            {var subQ0=sQuery(id+"F0.wireOp",EDGE,"E21.filletArc");var subQ1=sQuery(id+"F0.wireOp",EDGE,"E7");var subQ2=sQuery(id+"F0.wireOp",EDGE,"E6");var subQ3=sQuery(id+"F0.wireOp",EDGE,"E5");var subQ4=sQuery(id+"F0.wireOp",EDGE,"E4");var subQ5=sQuery(id+"F0.wireOp",EDGE,"E22.filletArc");var subQ6=sQuery(id+"F0.wireOp",EDGE,"E1.bottom");var subQ7=sQuery(id+"F0.wireOp",EDGE,"E1.right");var subQ8=sQuery(id+"F0.wireOp",EDGE,"E1.top");var subQ9=sQuery(id+"F0.wireOp",EDGE,"E1.left");var subQ10=sQuery(id+"F0.wireOp",EDGE,"E23.filletArc");var subQ11=sQuery(id+"F0.wireOp",EDGE,"E24.filletArc");Q0=makeQuery(id+"F2.boolean.opBoolean","SPLIT",FACE,{"disambiguationData":[TD([makeQuery(id+"F1.opExtrude","SWEPT_FACE",FACE,{"disambiguationData":[OSD([subQ6])]})])],"derivedFrom":makeQuery(id+"F1.opExtrude","CAP_FACE",FACE,{"disambiguationData":[OSD([subQ6,subQ8,subQ9,subQ7,subQ4,subQ3,subQ2,subQ1,subQ0,subQ5,subQ10,subQ11])],"isStart":true})});}
            var sketch = newSketch(context, id + "F16", { "sketchPlane" : qUnion([Q0])});
            skLineSegment(sketch, "E79", {"start": v(0, 90) * mm, "end": v(0, 120) * mm, "construction": true});
            skCircle(sketch, "E80", {"center": v(0, 120) * mm, "radius": 6 * mm});
            skLineSegment(sketch, "E81", {"start": v(15, 120) * mm, "end": v(15, 108) * mm});
            skLineSegment(sketch, "E82", {"start": v(15, 108) * mm, "end": v(33, 90) * mm});
            skLineSegment(sketch, "E83", {"start": v(-15, 120) * mm, "end": v(-15, 108) * mm});
            skArc(sketch, "E84", {"start": v(15, 120) * mm, "mid": v(0, 135) * mm, "end": v(-15, 120) * mm});
            skLineSegment(sketch, "E85", {"start": v(0, -90) * mm, "end": v(0, -104.25) * mm, "construction": true});
            skPoint(sketch, "E85.endSnap0", {"position": v(0, -90) * mm});
            skLineSegment(sketch, "E86", {"start": v(80, 0) * mm, "end": v(-80, 0) * mm, "construction": true});
            skLineSegment(sketch, "E87.MirrorCS", {"start": v(15, -120) * mm, "end": v(15, -108) * mm});
            skLineSegment(sketch, "E88.MirrorCS", {"start": v(-15, -120) * mm, "end": v(-15, -108) * mm});
            skArc(sketch, "E89.MirrorCS", {"start": v(15, -120) * mm, "mid": v(0, -135) * mm, "end": v(-15, -120) * mm});
            skCircle(sketch, "E90.MirrorC", {"center": v(0, -120) * mm, "radius": 6 * mm});
            skLineSegment(sketch, "E91", {"start": v(-15, 108) * mm, "end": v(-33, 90) * mm});
            skLineSegment(sketch, "E92.MirrorCS", {"start": v(15, -108) * mm, "end": v(33, -90) * mm});
            skLineSegment(sketch, "E93.MirrorCS", {"start": v(-15, -108) * mm, "end": v(-33, -90) * mm});
            skSolve(sketch);
        }
        {
            var Q0;
            Q0=makeQuery(id+"F16.imprint","IMPRINT",FACE,{"disambiguationData":[TD([[makeQuery(id+"F16.imprint","IMPRINT",EDGE,{"derivedFrom":sQuery(id+"F16.wireOp",EDGE,"E87.MirrorCS")}),1.0]])]});
            var Q1;
            Q1=makeQuery(id+"F16.imprint","IMPRINT",FACE,{"disambiguationData":[TD([[makeQuery(id+"F16.imprint","IMPRINT",EDGE,{"derivedFrom":sQuery(id+"F16.wireOp",EDGE,"E80")}),-1.0]])]});
            var Q2;
            Q2=makeQuery(id+"F2.opExtrude","CAP_FACE",FACE,{"disambiguationData":[OSD([sQuery(id+"F0.wireOp",EDGE,"E12"),sQuery(id+"F0.wireOp",EDGE,"E13"),sQuery(id+"F0.wireOp",EDGE,"E14"),sQuery(id+"F0.wireOp",EDGE,"E15"),sQuery(id+"F0.wireOp",EDGE,"E17.filletArc"),sQuery(id+"F0.wireOp",EDGE,"E18.filletArc"),sQuery(id+"F0.wireOp",EDGE,"E19.filletArc"),sQuery(id+"F0.wireOp",EDGE,"E20.filletArc"),sQuery(id+"F0.wireOp",EDGE,"E25.0"),sQuery(id+"F0.wireOp",EDGE,"E25.1"),sQuery(id+"F0.wireOp",EDGE,"E25.2"),sQuery(id+"F0.wireOp",EDGE,"E25.3"),sQuery(id+"F0.wireOp",EDGE,"E25.4"),sQuery(id+"F0.wireOp",EDGE,"E25.5"),sQuery(id+"F0.wireOp",EDGE,"E25.6"),sQuery(id+"F0.wireOp",EDGE,"E25.7")])],"isStart":false});
            extrude(context, id + "F17", {"entities" : qUnion([Q0, Q1]), "endBound" : BoundingType.UP_TO_SURFACE, "endBoundEntityFace" : qUnion([Q2]), "depth" : 25 * mm});
        }
    });
